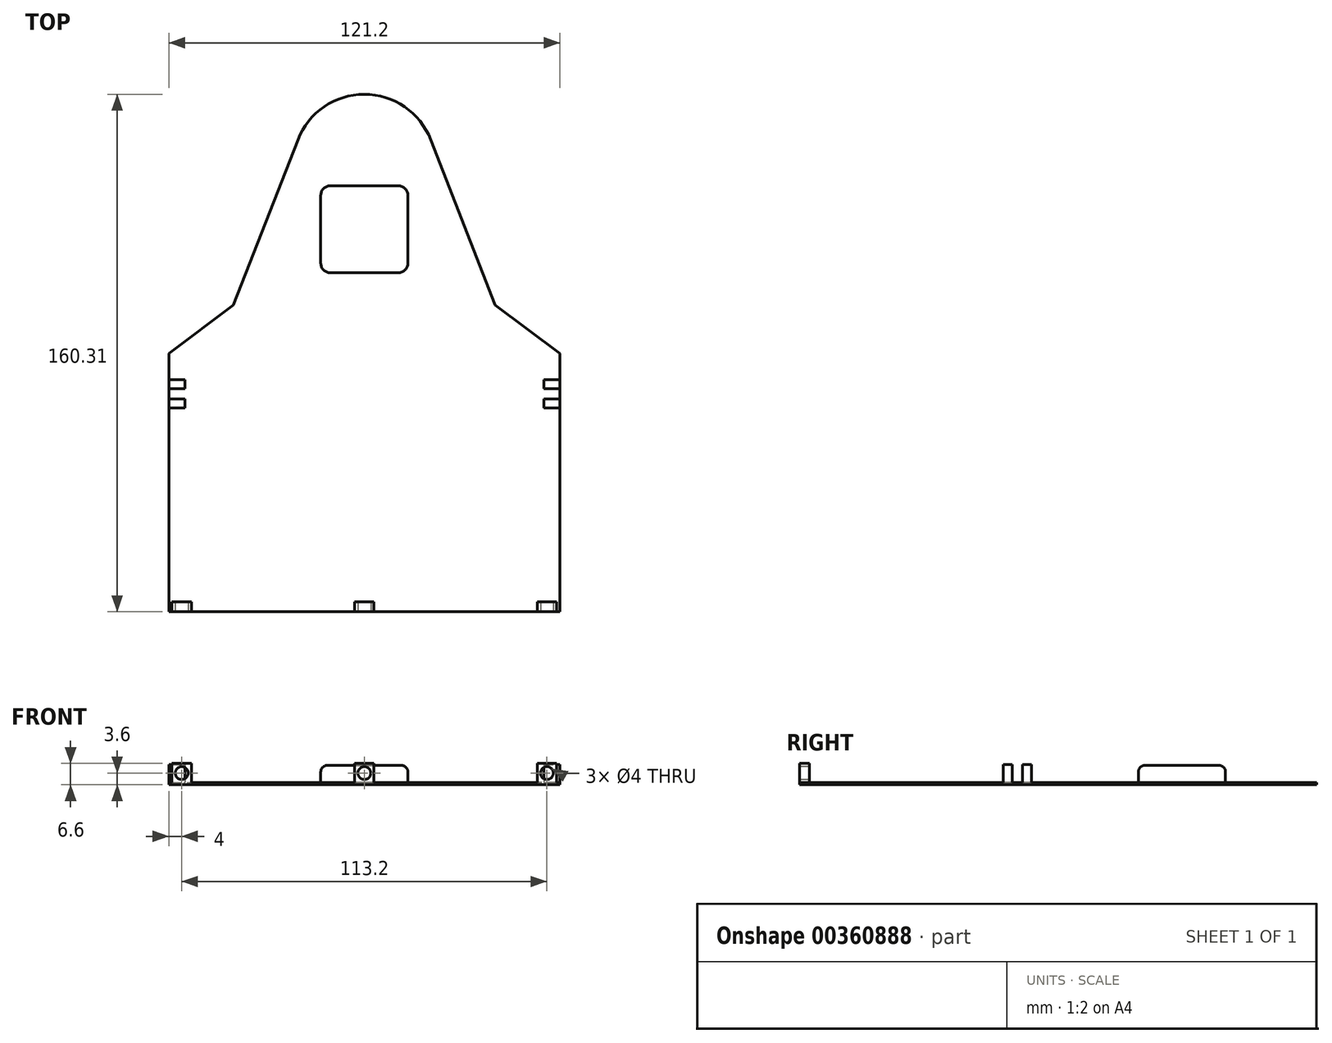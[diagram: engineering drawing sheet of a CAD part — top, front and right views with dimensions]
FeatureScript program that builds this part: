
annotation { "Feature Type Name" : "Feature", "Feature Type Description" : "" }
export const myFeature = defineFeature(function(context is Context, id is Id, definition is map)
    precondition{}
    {
        {
            var Q0;
            Q0=qCreatedBy(makeId("Top.planeOp"),FACE);
            var sketch = newSketch(context, id + "F0", { "sketchPlane" : qUnion([Q0])});
            skLineSegment(sketch, "E0", {"start": v(-60.6, 80) * mm, "end": v(-60.6, 0) * mm});
            skLineSegment(sketch, "E1", {"start": v(-60.6, 0) * mm, "end": v(60.6, 0) * mm});
            skLineSegment(sketch, "E2", {"start": v(60.6, 0) * mm, "end": v(60.6, 80) * mm});
            skLineSegment(sketch, "E3", {"start": v(60.6, 80) * mm, "end": v(40.6, 95) * mm});
            skLineSegment(sketch, "E4", {"start": v(40.6, 95) * mm, "end": v(20.6, 146.23) * mm});
            skLineSegment(sketch, "E5", {"start": v(-60.6, 80) * mm, "end": v(-40.6, 95) * mm});
            skLineSegment(sketch, "E6", {"start": v(-40.6, 95) * mm, "end": v(-20.6, 146.23) * mm});
            skArc(sketch, "E7", {"start": v(-20.6, 146.23) * mm, "mid": v(0, 160.3) * mm, "end": v(20.6, 146.23) * mm});
            skPoint(sketch, "E8", {"position": v(0, 0) * mm});
            skLineSegment(sketch, "E9.bottom", {"start": v(-13.5, 132) * mm, "end": v(13.5, 132) * mm});
            skLineSegment(sketch, "E9.top", {"start": v(-13.5, 105) * mm, "end": v(13.5, 105) * mm});
            skLineSegment(sketch, "E9.left", {"start": v(-13.5, 132) * mm, "end": v(-13.5, 105) * mm});
            skLineSegment(sketch, "E9.right", {"start": v(13.5, 132) * mm, "end": v(13.5, 105) * mm});
            skPoint(sketch, "E10", {"position": v(0, 105) * mm});
            skSolve(sketch);
        }
        {
            var Q0;
            Q0 = qSketchRegion(id + "F0", true);
            var Q1;
            Q1=makeQuery(id+"F0.imprint","IMPRINT",FACE,{"disambiguationData":[TD([[makeQuery(id+"F0.imprint","IMPRINT",EDGE,{"derivedFrom":sQuery(id+"F0.wireOp",EDGE,"E9.bottom")}),-1.0]])]});
            extrude(context, id + "F1", {"entities" : qUnion([Q0, Q1]), "depth" : 0.6 * mm});
        }
        {
            var Q0;
            Q0=makeQuery(id+"F0.imprint","IMPRINT",FACE,{"disambiguationData":[TD([[makeQuery(id+"F0.imprint","IMPRINT",EDGE,{"derivedFrom":sQuery(id+"F0.wireOp",EDGE,"E9.bottom")}),-1.0]])]});
            extrude(context, id + "F2", {"entities" : qUnion([Q0]), "operationType" : NewBodyOperationType.ADD, "depth" : 6 * mm});
        }
        {
            var Q0;
            Q0=makeQuery(id+"F2.opExtrude","CAP_FACE",FACE,{"disambiguationData":[OSD([sQuery(id+"F0.wireOp",EDGE,"E9.bottom"),sQuery(id+"F0.wireOp",EDGE,"E9.top"),sQuery(id+"F0.wireOp",EDGE,"E9.left"),sQuery(id+"F0.wireOp",EDGE,"E9.right")])],"isStart":false});
            fillet(context, id + "F3", {"entities" : qUnion([Q0]), "radius" : 2 * mm, "tangentPropagation" : true, "allowEdgeOverflow" : false});
        }
        {
            var Q0;
            Q0=makeQuery(id+"F2.opExtrude","SWEPT_EDGE",EDGE,{"disambiguationData":[OSD([sQuery(id+"F0.wireOp",EDGE,"E9.bottom"),sQuery(id+"F0.wireOp",EDGE,"E9.left")])]});
            var Q1;
            Q1=makeQuery(id+"F2.opExtrude","SWEPT_EDGE",EDGE,{"disambiguationData":[OSD([sQuery(id+"F0.wireOp",EDGE,"E9.top"),sQuery(id+"F0.wireOp",EDGE,"E9.left")])]});
            var Q2;
            Q2=makeQuery(id+"F2.opExtrude","SWEPT_EDGE",EDGE,{"disambiguationData":[OSD([sQuery(id+"F0.wireOp",EDGE,"E9.top"),sQuery(id+"F0.wireOp",EDGE,"E9.right")])]});
            var Q3;
            Q3=makeQuery(id+"F2.opExtrude","SWEPT_EDGE",EDGE,{"disambiguationData":[OSD([sQuery(id+"F0.wireOp",EDGE,"E9.bottom"),sQuery(id+"F0.wireOp",EDGE,"E9.right")])]});
            fillet(context, id + "F4", {"entities" : qUnion([Q0, Q1, Q2, Q3]), "radius" : 3 * mm, "tangentPropagation" : true, "allowEdgeOverflow" : false});
        }
        {
            var Q0;
            Q0=makeQuery(id+"F1.opExtrude","CAP_FACE",FACE,{"disambiguationData":[OSD([sQuery(id+"F0.wireOp",EDGE,"E0"),sQuery(id+"F0.wireOp",EDGE,"E1"),sQuery(id+"F0.wireOp",EDGE,"E2"),sQuery(id+"F0.wireOp",EDGE,"E3"),sQuery(id+"F0.wireOp",EDGE,"E4"),sQuery(id+"F0.wireOp",EDGE,"E5"),sQuery(id+"F0.wireOp",EDGE,"E6"),sQuery(id+"F0.wireOp",EDGE,"E7")])],"isStart":false});
            var sketch = newSketch(context, id + "F5", { "sketchPlane" : qUnion([Q0])});
            skLineSegment(sketch, "E11.bottom", {"start": v(-60.6, 71.9) * mm, "end": v(-55.6, 71.9) * mm});
            skLineSegment(sketch, "E11.top", {"start": v(-60.6, 69.1) * mm, "end": v(-55.6, 69.1) * mm});
            skLineSegment(sketch, "E11.left", {"start": v(-60.6, 71.9) * mm, "end": v(-60.6, 69.1) * mm});
            skLineSegment(sketch, "E11.right", {"start": v(-55.6, 71.9) * mm, "end": v(-55.6, 69.1) * mm});
            skLineSegment(sketch, "E12.bottom", {"start": v(-60.6, 65.9) * mm, "end": v(-55.6, 65.9) * mm});
            skLineSegment(sketch, "E12.top", {"start": v(-60.6, 63.1) * mm, "end": v(-55.6, 63.1) * mm});
            skLineSegment(sketch, "E12.left", {"start": v(-60.6, 65.9) * mm, "end": v(-60.6, 63.1) * mm});
            skLineSegment(sketch, "E12.right", {"start": v(-55.6, 65.9) * mm, "end": v(-55.6, 63.1) * mm});
            skLineSegment(sketch, "E13.bottom", {"start": v(55.6, 71.9) * mm, "end": v(60.6, 71.9) * mm});
            skLineSegment(sketch, "E13.top", {"start": v(55.6, 69.1) * mm, "end": v(60.6, 69.1) * mm});
            skLineSegment(sketch, "E13.left", {"start": v(55.6, 71.9) * mm, "end": v(55.6, 69.1) * mm});
            skLineSegment(sketch, "E13.right", {"start": v(60.6, 71.9) * mm, "end": v(60.6, 69.1) * mm});
            skLineSegment(sketch, "E14.bottom", {"start": v(55.6, 65.9) * mm, "end": v(60.6, 65.9) * mm});
            skLineSegment(sketch, "E14.top", {"start": v(55.6, 63.1) * mm, "end": v(60.6, 63.1) * mm});
            skLineSegment(sketch, "E14.left", {"start": v(55.6, 65.9) * mm, "end": v(55.6, 63.1) * mm});
            skLineSegment(sketch, "E14.right", {"start": v(60.6, 65.9) * mm, "end": v(60.6, 63.1) * mm});
            skSolve(sketch);
        }
        {
            var Q0;
            Q0 = qSketchRegion(id + "F5", true);
            extrude(context, id + "F6", {"entities" : qUnion([Q0]), "operationType" : NewBodyOperationType.ADD, "depth" : 5.6 * mm});
        }
        {
            var Q0;
            Q0=makeQuery(id+"F1.opExtrude","CAP_FACE",FACE,{"disambiguationData":[OSD([sQuery(id+"F0.wireOp",EDGE,"E0"),sQuery(id+"F0.wireOp",EDGE,"E1"),sQuery(id+"F0.wireOp",EDGE,"E2"),sQuery(id+"F0.wireOp",EDGE,"E3"),sQuery(id+"F0.wireOp",EDGE,"E4"),sQuery(id+"F0.wireOp",EDGE,"E5"),sQuery(id+"F0.wireOp",EDGE,"E6"),sQuery(id+"F0.wireOp",EDGE,"E7")])],"isStart":false});
            var sketch = newSketch(context, id + "F7", { "sketchPlane" : qUnion([Q0])});
            skLineSegment(sketch, "E15.bottom", {"start": v(-59.6, 0) * mm, "end": v(-53.6, 0) * mm});
            skLineSegment(sketch, "E15.top", {"start": v(-59.6, 3) * mm, "end": v(-53.6, 3) * mm});
            skLineSegment(sketch, "E15.left", {"start": v(-59.6, 0) * mm, "end": v(-59.6, 3) * mm});
            skLineSegment(sketch, "E15.right", {"start": v(-53.6, 0) * mm, "end": v(-53.6, 3) * mm});
            skLineSegment(sketch, "E16.bottom", {"start": v(59.6, 0) * mm, "end": v(53.6, 0) * mm});
            skLineSegment(sketch, "E16.top", {"start": v(59.6, 3) * mm, "end": v(53.6, 3) * mm});
            skLineSegment(sketch, "E16.left", {"start": v(59.6, 0) * mm, "end": v(59.6, 3) * mm});
            skLineSegment(sketch, "E16.right", {"start": v(53.6, 0) * mm, "end": v(53.6, 3) * mm});
            skLineSegment(sketch, "E17.bottom", {"start": v(-3, 3) * mm, "end": v(3, 3) * mm});
            skLineSegment(sketch, "E17.top", {"start": v(-3, 0) * mm, "end": v(3, 0) * mm});
            skLineSegment(sketch, "E17.left", {"start": v(-3, 3) * mm, "end": v(-3, 0) * mm});
            skLineSegment(sketch, "E17.right", {"start": v(3, 3) * mm, "end": v(3, 0) * mm});
            skPoint(sketch, "E18", {"position": v(0, 3) * mm});
            skSolve(sketch);
        }
        {
            var Q0;
            Q0 = qSketchRegion(id + "F7", true);
            extrude(context, id + "F8", {"entities" : qUnion([Q0]), "operationType" : NewBodyOperationType.ADD, "depth" : 6 * mm});
        }
        {
            var Q0;
            Q0=makeQuery(id+"F8.boolean.opBoolean","MERGE",FACE,{"derivedFrom":[makeQuery(id+"F1.opExtrude","SWEPT_FACE",FACE,{"disambiguationData":[OSD([sQuery(id+"F0.wireOp",EDGE,"E1")])]}),makeQuery(id+"F8.opExtrude","SWEPT_FACE",FACE,{"disambiguationData":[OSD([sQuery(id+"F7.wireOp",EDGE,"E15.bottom")])]}),makeQuery(id+"F8.opExtrude","SWEPT_FACE",FACE,{"disambiguationData":[OSD([sQuery(id+"F7.wireOp",EDGE,"E16.bottom")])]})]});
            var sketch = newSketch(context, id + "F9", { "sketchPlane" : qUnion([Q0])});
            skCircle(sketch, "E19", {"center": v(56.6, 3.6) * mm, "radius": 2 * mm});
            skCircle(sketch, "E20", {"center": v(-56.6, 3.6) * mm, "radius": 2 * mm});
            skCircle(sketch, "E21", {"center": v(0, 3.6) * mm, "radius": 2 * mm});
            skSolve(sketch);
        }
        {
            var Q0;
            Q0 = qSketchRegion(id + "F9", true);
            extrude(context, id + "F10", {"entities" : qUnion([Q0]), "operationType" : NewBodyOperationType.REMOVE, "oppositeDirection" : true, "depth" : 4 * mm});
        }
    });
